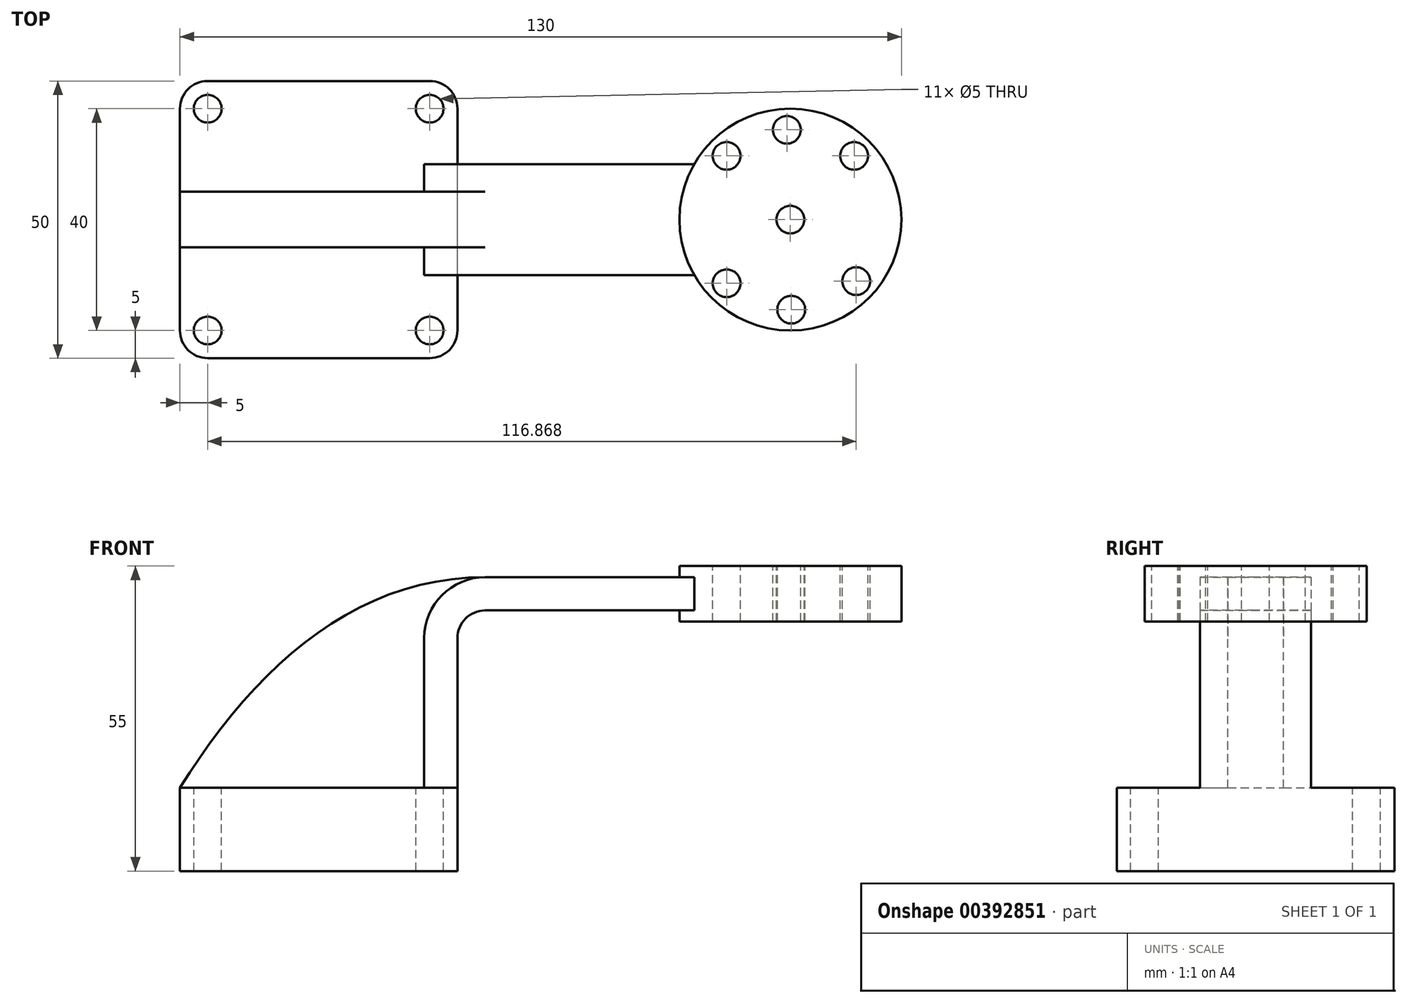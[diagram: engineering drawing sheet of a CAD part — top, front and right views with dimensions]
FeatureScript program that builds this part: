
annotation { "Feature Type Name" : "Feature", "Feature Type Description" : "" }
export const myFeature = defineFeature(function(context is Context, id is Id, definition is map)
    precondition{}
    {
        {
            var Q0;
            Q0=qCreatedBy(makeId("Front.planeOp"),FACE);
            var sketch = newSketch(context, id + "F0", { "sketchPlane" : qUnion([Q0])});
            skLineSegment(sketch, "E0.bottom", {"start": v(25, 7.5) * mm, "end": v(-25, 7.5) * mm});
            skLineSegment(sketch, "E0.top", {"start": v(25, -7.5) * mm, "end": v(-25, -7.5) * mm});
            skLineSegment(sketch, "E0.left", {"start": v(25, 7.5) * mm, "end": v(25, -7.5) * mm});
            skLineSegment(sketch, "E0.right", {"start": v(-25, 7.5) * mm, "end": v(-25, -7.5) * mm});
            skPoint(sketch, "E0.middle", {"position": v(0, 0) * mm});
            skLineSegment(sketch, "E1.bottom", {"start": v(105, 37.5) * mm, "end": v(65, 37.5) * mm});
            skLineSegment(sketch, "E1.top", {"start": v(105, 47.5) * mm, "end": v(65, 47.5) * mm});
            skLineSegment(sketch, "E1.left", {"start": v(105, 37.5) * mm, "end": v(105, 47.5) * mm});
            skLineSegment(sketch, "E1.right", {"start": v(65, 37.5) * mm, "end": v(65, 47.5) * mm});
            skPoint(sketch, "E1.middle", {"position": v(85, 42.5) * mm});
            skLineSegment(sketch, "E2", {"start": v(25, 7.5) * mm, "end": v(25, 34.5) * mm});
            skArc(sketch, "E3", {"start": v(25, 34.5) * mm, "mid": v(26.46, 38.04) * mm, "end": v(30, 39.5) * mm});
            skLineSegment(sketch, "E4", {"start": v(30, 39.5) * mm, "end": v(85, 39.5) * mm});
            skLineSegment(sketch, "E5.0", {"start": v(30, 45.5) * mm, "end": v(85, 45.5) * mm});
            skArc(sketch, "E5.1", {"start": v(19, 34.5) * mm, "mid": v(22.22, 42.28) * mm, "end": v(30, 45.5) * mm});
            skLineSegment(sketch, "E5.2", {"start": v(19, 7.5) * mm, "end": v(19, 34.5) * mm});
            skLineSegment(sketch, "E6", {"start": v(85, 37.5) * mm, "end": v(85, 47.5) * mm});
            skLineSegment(sketch, "E7", {"start": v(19, 7.5) * mm, "end": v(25, 7.5) * mm});
            skFitSpline(sketch, "E8", {"points": [v(-25, 7.5) * mm, v(30, 45.5) * mm], "startDerivative": vector(39.92, 64.71) * mm, "endDerivative": vector(70.67, -0.12) * mm});
            skSolve(sketch);
        }
        {
            var Q0;
            Q0=makeQuery(id+"F0.imprint","IMPRINT",FACE,{"disambiguationData":[TD([[makeQuery(id+"F0.imprint","IMPRINT",EDGE,{"derivedFrom":sQuery(id+"F0.wireOp",EDGE,"E0.bottom")}),1.0]])]});
            extrude(context, id + "F1", {"entities" : qUnion([Q0]), "endBound" : BoundingType.SYMMETRIC, "depth" : 50 * mm});
        }
        {
            var Q0;
            Q0=makeQuery(id+"F0.imprint","IMPRINT",FACE,{"disambiguationData":[TD([[makeQuery(id+"F0.imprint","IMPRINT",EDGE,{"derivedFrom":sQuery(id+"F0.wireOp",EDGE,"E0.bottom")}),-1.0]])]});
            extrude(context, id + "F2", {"entities" : qUnion([Q0]), "operationType" : NewBodyOperationType.ADD, "endBound" : BoundingType.SYMMETRIC, "depth" : 10 * mm});
        }
        {
            var Q0;
            Q0=makeQuery(id+"F0.imprint","IMPRINT",FACE,{"disambiguationData":[TD([[makeQuery(id+"F0.imprint","IMPRINT",EDGE,{"derivedFrom":sQuery(id+"F0.wireOp",EDGE,"E2")}),1.0]])]});
            var Q1;
            {var subQ0=sQuery(id+"F0.wireOp",EDGE,"E4");var subQ1=sQuery(id+"F0.wireOp",EDGE,"E1.right");var subQ2=makeQuery(id+"F0.imprint","INTERSECT",VERTEX,{"derivedFrom":[subQ1,subQ0]});Q1=makeQuery(id+"F0.imprint","IMPRINT",FACE,{"disambiguationData":[TD([[makeQuery(id+"F0.imprint","IMPRINT",EDGE,{"disambiguationData":[TD([[subQ2,-1.0]])],"derivedFrom":subQ1}),-1.0]])]});}
            extrude(context, id + "F3", {"entities" : qUnion([Q0, Q1]), "operationType" : NewBodyOperationType.ADD, "endBound" : BoundingType.SYMMETRIC, "depth" : 20 * mm});
        }
        {
            var Q0;
            {var subQ4=sQuery(id+"F0.wireOp",EDGE,"E1.left");Q0=makeQuery(id+"F0.imprint","IMPRINT",FACE,{"disambiguationData":[TD([[makeQuery(id+"F0.imprint","IMPRINT",EDGE,{"derivedFrom":subQ4}),1.0]])]});}
            var Q1;
            Q1=sQuery(id+"F0.wireOp",EDGE,"E6");
            revolve(context, id + "F4", {"operationType" : NewBodyOperationType.ADD, "entities" : qUnion([Q0]), "axis" : qUnion([Q1]), "revolveType" : RevolveType.FULL});
        }
        {
            var Q0;
            Q0=makeQuery(id+"F1.opExtrude","CAP_EDGE",EDGE,{"disambiguationData":[OSD([sQuery(id+"F0.wireOp",EDGE,"E0.left")])],"isStart":true});
            var Q1;
            Q1=makeQuery(id+"F1.opExtrude","CAP_EDGE",EDGE,{"disambiguationData":[OSD([sQuery(id+"F0.wireOp",EDGE,"E0.right")])],"isStart":true});
            var Q2;
            Q2=makeQuery(id+"F1.opExtrude","CAP_EDGE",EDGE,{"disambiguationData":[OSD([sQuery(id+"F0.wireOp",EDGE,"E0.left")])],"isStart":false});
            var Q3;
            Q3=makeQuery(id+"F1.opExtrude","CAP_EDGE",EDGE,{"disambiguationData":[OSD([sQuery(id+"F0.wireOp",EDGE,"E0.right")])],"isStart":false});
            fillet(context, id + "F5", {"entities" : qUnion([Q0, Q1, Q2, Q3]), "radius" : 5 * mm, "tangentPropagation" : true, "allowEdgeOverflow" : false});
        }
        {
            var Q0;
            {var subQ0=sQuery(id+"F0.wireOp",EDGE,"E8");var subQ1=sQuery(id+"F0.wireOp",EDGE,"E5.2");var subQ2=sQuery(id+"F0.wireOp",EDGE,"E5.1");var subQ3=sQuery(id+"F0.wireOp",EDGE,"E0.bottom");var subQ6=sQuery(id+"F0.wireOp",EDGE,"E7");Q0=makeQuery(id+"F3.boolean.opBoolean","SPLIT",FACE,{"disambiguationData":[TD([makeQuery(id+"F2.opExtrude","CAP_FACE",FACE,{"disambiguationData":[OSD([subQ3,subQ2,subQ1,subQ0])],"isStart":true})])],"derivedFrom":makeQuery(id+"F1.opExtrude","SWEPT_FACE",FACE,{"disambiguationData":[OSD([subQ3,subQ6])]})});}
            var sketch = newSketch(context, id + "F6", { "sketchPlane" : qUnion([Q0])});
            skCircle(sketch, "E9", {"center": v(-20, -20) * mm, "radius": 2.5 * mm});
            skCircle(sketch, "E10", {"center": v(20, -20) * mm, "radius": 2.5 * mm});
            skCircle(sketch, "E11", {"center": v(-20, 20) * mm, "radius": 2.5 * mm});
            skCircle(sketch, "E12", {"center": v(20, 20) * mm, "radius": 2.5 * mm});
            skSolve(sketch);
        }
        {
            var Q0;
            Q0=sQuery(id+"F6.wireOp",VERTEX,"E12.center");
            var Q1;
            Q1=sQuery(id+"F6.wireOp",VERTEX,"E11.center");
            var Q2;
            Q2=sQuery(id+"F6.wireOp",VERTEX,"E10.center");
            var Q3;
            Q3=sQuery(id+"F6.wireOp",VERTEX,"E9.center");
            var Q4;
            Q4=makeQuery(id+"F1.opExtrude","SWEPT_BODY",BODY,{"disambiguationData":[OSD([sQuery(id+"F0.wireOp",EDGE,"E0.bottom"),sQuery(id+"F0.wireOp",EDGE,"E0.top"),sQuery(id+"F0.wireOp",EDGE,"E0.left"),sQuery(id+"F0.wireOp",EDGE,"E0.right"),sQuery(id+"F0.wireOp",EDGE,"E7")])]});
            hole(context, id + "F7", {"style" : HoleStyle.SIMPLE, "endStyle" : HoleEndStyle.THROUGH, "holeDiameter" : 5 * mm, "isTappedThrough" : true, "tappedDepth" : 12 * mm, "tapClearance" : 3, "locations" : qUnion([Q0, Q1, Q2, Q3]), "scope" : qUnion([Q4])});
        }
        {
            var Q0;
            Q0=makeQuery(id+"F4.opRevolve","SWEPT_FACE",FACE,{"disambiguationData":[OSD([sQuery(id+"F0.wireOp",EDGE,"E1.top")])]});
            var sketch = newSketch(context, id + "F8", { "sketchPlane" : qUnion([Q0])});
            skCircle(sketch, "E13", {"center": v(85, 0) * mm, "radius": 2.5 * mm});
            skArc(sketch, "E14", {"start": v(98.26, 13.26) * mm, "mid": v(85, 18.75) * mm, "end": v(71.74, 13.26) * mm});
            skArc(sketch, "E15", {"start": v(94.72, 9.72) * mm, "mid": v(85, 13.75) * mm, "end": v(75.28, 9.72) * mm});
            skArc(sketch, "E16", {"start": v(94.72, 9.72) * mm, "mid": v(98.26, 9.72) * mm, "end": v(98.26, 13.26) * mm});
            skArc(sketch, "E17", {"start": v(71.74, 13.26) * mm, "mid": v(71.74, 9.72) * mm, "end": v(75.28, 9.72) * mm});
            skArc(sketch, "E18", {"start": v(98.64, -12.87) * mm, "mid": v(98.58, -9.27) * mm, "end": v(94.99, -9.45) * mm});
            skArc(sketch, "E19", {"start": v(75.28, -9.72) * mm, "mid": v(71.74, -9.72) * mm, "end": v(71.74, -13.26) * mm});
            skPoint(sketch, "E20.orphan", {"position": v(95.1, -9.33) * mm});
            skArc(sketch, "E21.trimOffspring", {"start": v(75.28, -9.72) * mm, "mid": v(85.27, -13.75) * mm, "end": v(95.1, -9.33) * mm});
            skArc(sketch, "E22.trimOffspring", {"start": v(71.74, -13.26) * mm, "mid": v(85.36, -18.75) * mm, "end": v(98.75, -12.75) * mm});
            skCircle(sketch, "E23", {"center": v(85.16, -16.25) * mm, "radius": 2.5 * mm});
            skCircle(sketch, "E24", {"center": v(84.37, 16.2) * mm, "radius": 2.5 * mm});
            skSolve(sketch);
        }
        {
            var Q0;
            Q0=sQuery(id+"F8.wireOp",VERTEX,"E15.center");
            var Q1;
            Q1=sQuery(id+"F8.wireOp",VERTEX,"E17.center");
            var Q2;
            Q2=sQuery(id+"F8.wireOp",VERTEX,"E16.center");
            var Q3;
            Q3=sQuery(id+"F8.wireOp",VERTEX,"E19.center");
            var Q4;
            Q4=sQuery(id+"F8.wireOp",VERTEX,"E18.center");
            var Q5;
            Q5=sQuery(id+"F8.wireOp",VERTEX,"E23.center");
            var Q6;
            Q6=sQuery(id+"F8.wireOp",VERTEX,"E24.center");
            var Q7;
            Q7=makeQuery(id+"F1.opExtrude","SWEPT_BODY",BODY,{"disambiguationData":[OSD([sQuery(id+"F0.wireOp",EDGE,"E0.bottom"),sQuery(id+"F0.wireOp",EDGE,"E0.top"),sQuery(id+"F0.wireOp",EDGE,"E0.left"),sQuery(id+"F0.wireOp",EDGE,"E0.right"),sQuery(id+"F0.wireOp",EDGE,"E7")])]});
            hole(context, id + "F9", {"style" : HoleStyle.SIMPLE, "endStyle" : HoleEndStyle.THROUGH, "holeDiameter" : 5 * mm, "isTappedThrough" : true, "tappedDepth" : 12 * mm, "tapClearance" : 3, "locations" : qUnion([Q0, Q1, Q2, Q3, Q4, Q5, Q6]), "scope" : qUnion([Q7])});
        }
    });
